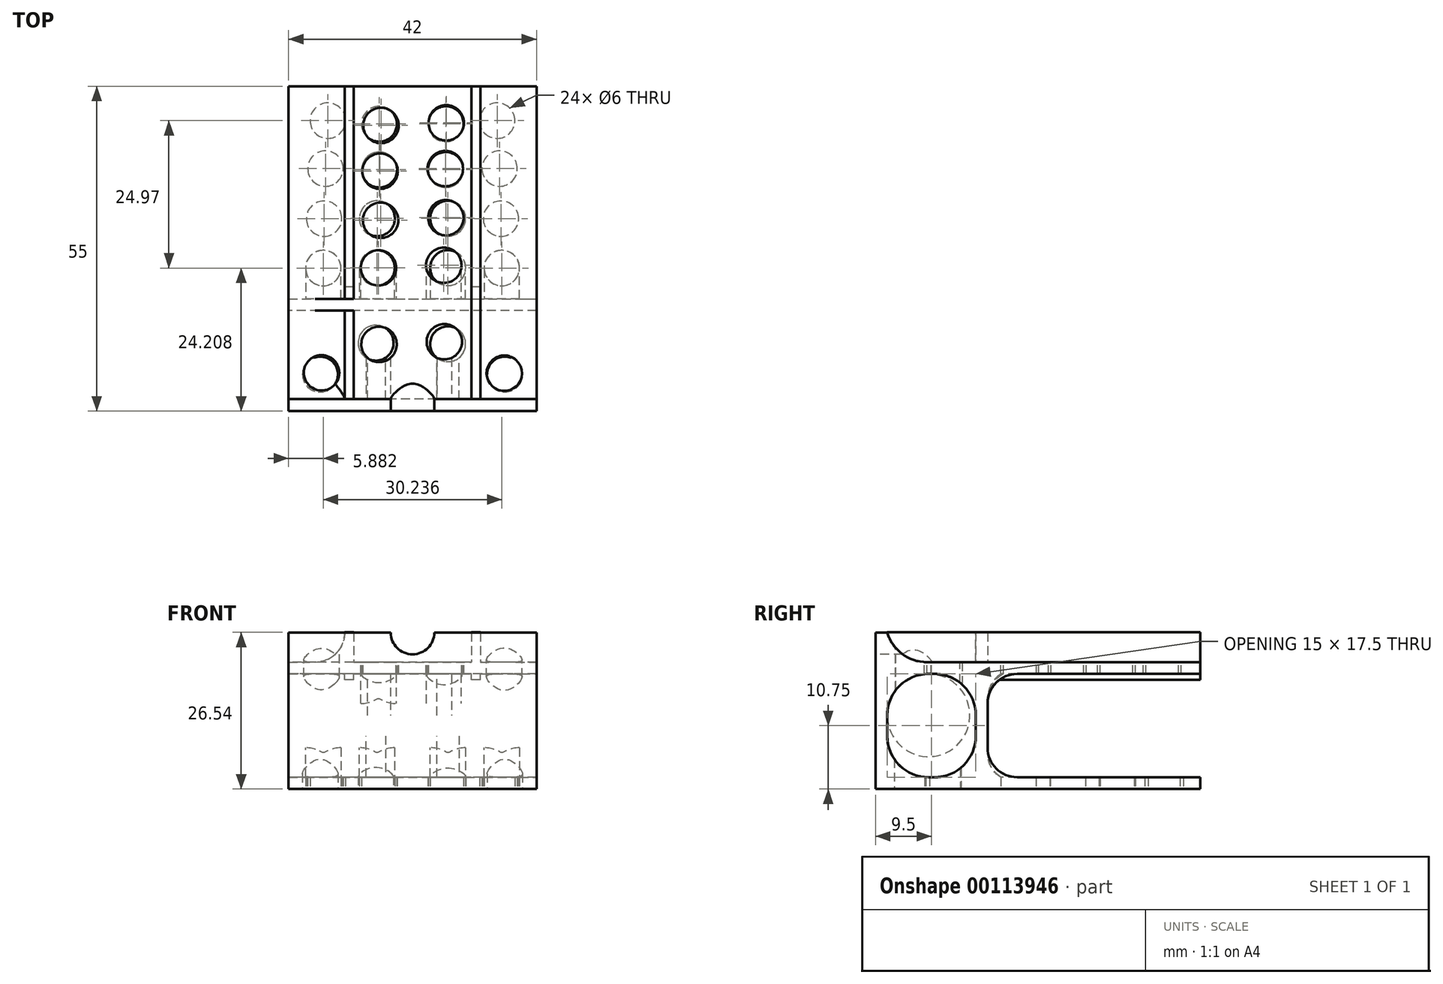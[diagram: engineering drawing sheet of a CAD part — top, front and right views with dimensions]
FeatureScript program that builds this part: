
annotation { "Feature Type Name" : "Feature", "Feature Type Description" : "" }
export const myFeature = defineFeature(function(context is Context, id is Id, definition is map)
    precondition{}
    {
        {
            var Q0;
            Q0=qCreatedBy(makeId("Front.planeOp"),FACE);
            var sketch = newSketch(context, id + "F0", { "sketchPlane" : qUnion([Q0])});
            skLineSegment(sketch, "E0.top", {"start": v(21, 15.75) * mm, "end": v(3.68, 15.75) * mm});
            skLineSegment(sketch, "E0.left", {"start": v(21, -10.75) * mm, "end": v(21, 15.75) * mm});
            skLineSegment(sketch, "E0.right", {"start": v(-21, -10.75) * mm, "end": v(-21, 15.75) * mm});
            skPoint(sketch, "E0.middle", {"position": v(0, 0) * mm});
            skLineSegment(sketch, "E1.bottom", {"start": v(21, -8.75) * mm, "end": v(-21, -8.75) * mm});
            skLineSegment(sketch, "E1.top", {"start": v(21, 8.75) * mm, "end": v(-21, 8.75) * mm});
            skLineSegment(sketch, "E1.left", {"start": v(21, -8.75) * mm, "end": v(21, 8.75) * mm});
            skLineSegment(sketch, "E1.right", {"start": v(-21, -8.75) * mm, "end": v(-21, 8.75) * mm});
            skLineSegment(sketch, "E2.bottom", {"start": v(21, -10.75) * mm, "end": v(-21, -10.75) * mm});
            skLineSegment(sketch, "E2.top", {"start": v(21, 10.75) * mm, "end": v(-21, 10.75) * mm});
            skLineSegment(sketch, "E2.left", {"start": v(21, -10.75) * mm, "end": v(21, 10.75) * mm});
            skLineSegment(sketch, "E2.right", {"start": v(-21, -10.75) * mm, "end": v(-21, 10.75) * mm});
            skArc(sketch, "E3", {"start": v(-3.68, 15.75) * mm, "mid": v(0, 12.07) * mm, "end": v(3.68, 15.75) * mm});
            skLineSegment(sketch, "E4.trimOffspring", {"start": v(-3.68, 15.75) * mm, "end": v(-21, 15.75) * mm});
            skPoint(sketch, "E5.orphan", {"position": v(-21, -15.75) * mm});
            skPoint(sketch, "E6.orphan", {"position": v(21, -15.75) * mm});
            skSolve(sketch);
        }
        {
            var Q0;
            Q0=qSketchRegion(id+"F0",true);
            extrude(context, id + "F1", {"entities" : qUnion([Q0]), "oppositeDirection" : true, "depth" : 2 * mm});
        }
        {
            var Q0;
            {var subQ0=sQuery(id+"F0.wireOp",EDGE,"E1.top");Q0=makeQuery(id+"F0.imprint","IMPRINT",FACE,{"disambiguationData":[TD([[makeQuery(id+"F0.imprint","IMPRINT",EDGE,{"derivedFrom":subQ0}),-1.0]])]});}
            var Q1;
            {var subQ0=sQuery(id+"F0.wireOp",EDGE,"E1.bottom");Q1=makeQuery(id+"F0.imprint","IMPRINT",FACE,{"disambiguationData":[TD([[makeQuery(id+"F0.imprint","IMPRINT",EDGE,{"derivedFrom":subQ0}),1.0]])]});}
            extrude(context, id + "F2", {"entities" : qUnion([Q0, Q1]), "operationType" : NewBodyOperationType.ADD, "oppositeDirection" : true, "depth" : 55 * mm});
        }
        {
            var Q0;
            Q0=makeQuery(id+"F2.opExtrude","SWEPT_FACE",FACE,{"disambiguationData":[OSD([sQuery(id+"F0.wireOp",EDGE,"E2.top")])]});
            var sketch = newSketch(context, id + "F3", { "sketchPlane" : qUnion([Q0])});
            skLineSegment(sketch, "E7.bottom", {"start": v(21, 2) * mm, "end": v(-21, 2) * mm});
            skLineSegment(sketch, "E7.top", {"start": v(21, 17) * mm, "end": v(-21, 17) * mm});
            skPoint(sketch, "E7.middle", {"position": v(0, 9.5) * mm});
            skLineSegment(sketch, "E8", {"start": v(-21, 19) * mm, "end": v(21, 19) * mm});
            skLineSegment(sketch, "E9", {"start": v(0, 55) * mm, "end": v(0, 0) * mm, "construction": true});
            skLineSegment(sketch, "E10.bottom", {"start": v(-11.49, 55) * mm, "end": v(-9.99, 55) * mm});
            skLineSegment(sketch, "E10.top", {"start": v(-11.49, 19) * mm, "end": v(-9.99, 19) * mm});
            skLineSegment(sketch, "E10.left", {"start": v(-11.49, 55) * mm, "end": v(-11.49, 19) * mm});
            skLineSegment(sketch, "E10.right", {"start": v(-9.99, 55) * mm, "end": v(-9.99, 19) * mm});
            skLineSegment(sketch, "E11.MirrorCS", {"start": v(9.99, 55) * mm, "end": v(9.99, 19) * mm});
            skLineSegment(sketch, "E12.MirrorCS", {"start": v(11.49, 55) * mm, "end": v(11.49, 19) * mm});
            skPoint(sketch, "E13.start.orphan", {"position": v(-19, 55) * mm});
            skPoint(sketch, "E14.MirrorCS.start.orphan", {"position": v(19, 55) * mm});
            skPoint(sketch, "E15.start.orphan", {"position": v(19, 19) * mm});
            skPoint(sketch, "E16.start.orphan", {"position": v(-19, 19) * mm});
            skLineSegment(sketch, "E17", {"start": v(-9.99, 19) * mm, "end": v(-9.99, 0) * mm});
            skLineSegment(sketch, "E18", {"start": v(-11.49, 19) * mm, "end": v(-11.49, 0) * mm});
            skLineSegment(sketch, "E19", {"start": v(9.99, 19) * mm, "end": v(9.99, 0) * mm});
            skLineSegment(sketch, "E20", {"start": v(11.49, 19) * mm, "end": v(11.49, 0) * mm});
            skSolve(sketch);
        }
        {
            var Q0;
            {var subQ0=sQuery(id+"F3.wireOp",EDGE,"E7.top");Q0=makeQuery(id+"F3.imprint","IMPRINT",FACE,{"disambiguationData":[TD([[makeQuery(id+"F3.imprint","IMPRINT",EDGE,{"derivedFrom":subQ0}),-1.0]])]});}
            var Q1;
            {var subQ0=sQuery(id+"F3.wireOp",EDGE,"E10.top");Q1=makeQuery(id+"F3.imprint","IMPRINT",FACE,{"disambiguationData":[TD([[makeQuery(id+"F3.imprint","IMPRINT",EDGE,{"derivedFrom":subQ0}),-1.0]])]});}
            extrude(context, id + "F4", {"entities" : qUnion([Q0, Q1]), "operationType" : NewBodyOperationType.ADD, "oppositeDirection" : true, "depth" : 21.22 * mm});
        }
        {
            var Q0;
            Q0=makeQuery(id+"F3.imprint","IMPRINT",FACE,{"disambiguationData":[TD([[makeQuery(id+"F3.imprint","IMPRINT",EDGE,{"derivedFrom":sQuery(id+"F3.wireOp",EDGE,"E10.bottom")}),1.0]])]});
            var Q1;
            {var subQ0=sQuery(id+"F3.wireOp",EDGE,"E11.MirrorCS");Q1=makeQuery(id+"F3.imprint","IMPRINT",FACE,{"disambiguationData":[TD([[makeQuery(id+"F3.imprint","IMPRINT",EDGE,{"derivedFrom":subQ0}),1.0]])]});}
            extrude(context, id + "F5", {"entities" : qUnion([Q0, Q1]), "operationType" : NewBodyOperationType.ADD, "oppositeDirection" : true, "depth" : 3 * mm});
        }
        {
            var Q0;
            {var subQ2=sQuery(id+"F0.wireOp",EDGE,"E2.bottom");Q0=makeQuery(id+"F4.boolean.opBoolean","SPLIT",FACE,{"disambiguationData":[TD([makeQuery(id+"F4.opExtrude","SWEPT_FACE",FACE,{"disambiguationData":[OSD([sQuery(id+"F3.wireOp",EDGE,"E8"),sQuery(id+"F3.wireOp",EDGE,"E10.top")])]})])],"derivedFrom":makeQuery(id+"F2.opExtrude","SWEPT_FACE",FACE,{"disambiguationData":[OSD([subQ2])]})});}
            var sketch = newSketch(context, id + "F6", { "sketchPlane" : qUnion([Q0])});
            skCircle(sketch, "E21", {"center": v(-15.12, -24.2) * mm, "radius": 3 * mm});
            skCircle(sketch, "E22", {"center": v(-6, -24.24) * mm, "radius": 3 * mm});
            skCircle(sketch, "E23", {"center": v(-14.98, -32.58) * mm, "radius": 3 * mm});
            skCircle(sketch, "E24", {"center": v(-6, -32.6) * mm, "radius": 3 * mm});
            skCircle(sketch, "E25", {"center": v(-5.62, -40.86) * mm, "radius": 3 * mm});
            skCircle(sketch, "E26", {"center": v(-14.75, -41.06) * mm, "radius": 3 * mm});
            skCircle(sketch, "E27", {"center": v(-14.35, -49.18) * mm, "radius": 3 * mm});
            skCircle(sketch, "E28", {"center": v(-5.65, -48.61) * mm, "radius": 3 * mm});
            skCircle(sketch, "E29", {"center": v(-15.63, -6.2) * mm, "radius": 3 * mm});
            skLineSegment(sketch, "E30", {"start": v(0, 29.9) * mm, "end": v(0, -70.72) * mm, "construction": true});
            skCircle(sketch, "E31.MirrorC", {"center": v(5.65, -48.61) * mm, "radius": 3 * mm});
            skCircle(sketch, "E32.MirrorC", {"center": v(14.35, -49.18) * mm, "radius": 3 * mm});
            skCircle(sketch, "E33.MirrorC", {"center": v(14.75, -41.06) * mm, "radius": 3 * mm});
            skCircle(sketch, "E34.MirrorC", {"center": v(5.62, -40.86) * mm, "radius": 3 * mm});
            skCircle(sketch, "E35.MirrorC", {"center": v(6, -32.6) * mm, "radius": 3 * mm});
            skCircle(sketch, "E36.MirrorC", {"center": v(14.98, -32.58) * mm, "radius": 3 * mm});
            skCircle(sketch, "E37.MirrorC", {"center": v(15.12, -24.2) * mm, "radius": 3 * mm});
            skCircle(sketch, "E38.MirrorC", {"center": v(6, -24.24) * mm, "radius": 3 * mm});
            skCircle(sketch, "E39.MirrorC", {"center": v(15.63, -6.2) * mm, "radius": 3 * mm});
            skCircle(sketch, "E40", {"center": v(-6.21, -11.52) * mm, "radius": 3 * mm});
            skCircle(sketch, "E41", {"center": v(6, -11.35) * mm, "radius": 3 * mm});
            skSolve(sketch);
        }
        {
            var Q0;
            Q0=qSketchRegion(id+"F6",true);
            extrude(context, id + "F7", {"entities" : qUnion([Q0]), "operationType" : NewBodyOperationType.REMOVE, "oppositeDirection" : true, "depth" : 10 * mm});
        }
        {
            var Q0;
            {var subQ0=sQuery(id+"F3.wireOp",EDGE,"E10.right");Q0=makeQuery(id+"F3.imprint","IMPRINT",FACE,{"disambiguationData":[TD([[makeQuery(id+"F3.imprint","IMPRINT",EDGE,{"derivedFrom":subQ0}),1.0]])]});}
            var sketch = newSketch(context, id + "F8", { "sketchPlane" : qUnion([Q0])});
            skCircle(sketch, "E42", {"center": v(5.72, 48.8) * mm, "radius": 3 * mm});
            skCircle(sketch, "E43", {"center": v(-5.35, 48.36) * mm, "radius": 3 * mm});
            skCircle(sketch, "E44", {"center": v(5.56, 41.05) * mm, "radius": 3 * mm});
            skCircle(sketch, "E45", {"center": v(-5.5, 40.6) * mm, "radius": 3 * mm});
            skCircle(sketch, "E46", {"center": v(5.65, 32.74) * mm, "radius": 3 * mm});
            skCircle(sketch, "E47", {"center": v(-5.41, 32.3) * mm, "radius": 3 * mm});
            skCircle(sketch, "E48", {"center": v(5.3, 24.69) * mm, "radius": 3 * mm});
            skCircle(sketch, "E49", {"center": v(-5.76, 24.24) * mm, "radius": 3 * mm});
            skCircle(sketch, "E50", {"center": v(5.39, 11.73) * mm, "radius": 3 * mm});
            skCircle(sketch, "E51", {"center": v(-5.67, 11.29) * mm, "radius": 3 * mm});
            skCircle(sketch, "E52", {"center": v(-15.4, 6.47) * mm, "radius": 3 * mm});
            skCircle(sketch, "E53", {"center": v(15.54, 6.4) * mm, "radius": 3 * mm});
            skSolve(sketch);
        }
        {
            var Q0;
            Q0=qSketchRegion(id+"F8",true);
            extrude(context, id + "F9", {"entities" : qUnion([Q0]), "operationType" : NewBodyOperationType.REMOVE, "oppositeDirection" : true, "depth" : 10 * mm});
        }
        {
            var Q0;
            {var subQ0=sQuery(id+"F3.wireOp",EDGE,"E20");var subQ1=sQuery(id+"F3.wireOp",EDGE,"E7.bottom");var subQ2=makeQuery(id+"F3.imprint","INTERSECT",VERTEX,{"derivedFrom":[subQ1,subQ0]});Q0=makeQuery(id+"F3.imprint","IMPRINT",FACE,{"disambiguationData":[TD([[makeQuery(id+"F3.imprint","IMPRINT",EDGE,{"disambiguationData":[TD([[subQ2,-1.0]])],"derivedFrom":subQ1}),-1.0]])]});}
            var Q1;
            {var subQ0=sQuery(id+"F3.wireOp",EDGE,"E11.MirrorCS");Q1=makeQuery(id+"F3.imprint","IMPRINT",FACE,{"disambiguationData":[TD([[makeQuery(id+"F3.imprint","IMPRINT",EDGE,{"derivedFrom":subQ0}),1.0]])]});}
            var Q2;
            {var subQ0=sQuery(id+"F3.wireOp",EDGE,"E20");var subQ1=sQuery(id+"F3.wireOp",EDGE,"E7.top");var subQ2=makeQuery(id+"F3.imprint","INTERSECT",VERTEX,{"derivedFrom":[subQ1,subQ0]});Q2=makeQuery(id+"F3.imprint","IMPRINT",FACE,{"disambiguationData":[TD([[makeQuery(id+"F3.imprint","IMPRINT",EDGE,{"disambiguationData":[TD([[subQ2,-1.0]])],"derivedFrom":subQ1}),-1.0]])]});}
            var Q3;
            {var subQ0=sQuery(id+"F3.wireOp",EDGE,"E17");var subQ1=sQuery(id+"F3.wireOp",EDGE,"E7.bottom");var subQ2=makeQuery(id+"F3.imprint","INTERSECT",VERTEX,{"derivedFrom":[subQ1,subQ0]});Q3=makeQuery(id+"F3.imprint","IMPRINT",FACE,{"disambiguationData":[TD([[makeQuery(id+"F3.imprint","IMPRINT",EDGE,{"disambiguationData":[TD([[subQ2,-1.0]])],"derivedFrom":subQ1}),-1.0]])]});}
            var Q4;
            {var subQ5=sQuery(id+"F3.wireOp",EDGE,"E10.top");Q4=makeQuery(id+"F3.imprint","IMPRINT",FACE,{"disambiguationData":[TD([[makeQuery(id+"F3.imprint","IMPRINT",EDGE,{"derivedFrom":subQ5}),-1.0]])]});}
            var Q5;
            Q5=makeQuery(id+"F3.imprint","IMPRINT",FACE,{"disambiguationData":[TD([[makeQuery(id+"F3.imprint","IMPRINT",EDGE,{"derivedFrom":sQuery(id+"F3.wireOp",EDGE,"E10.bottom")}),1.0]])]});
            extrude(context, id + "F10", {"entities" : qUnion([Q0, Q1, Q2, Q3, Q4, Q5]), "operationType" : NewBodyOperationType.ADD, "depth" : 5.04 * mm});
        }
        {
            var Q0;
            Q0=makeQuery(id+"F4.boolean.opBoolean","INTERSECT",EDGE,{"derivedFrom":[makeQuery(id+"F2.opExtrude","SWEPT_FACE",FACE,{"disambiguationData":[OSD([sQuery(id+"F0.wireOp",EDGE,"E1.bottom")])]}),makeQuery(id+"F4.opExtrude","SWEPT_FACE",FACE,{"disambiguationData":[OSD([sQuery(id+"F3.wireOp",EDGE,"E7.top")])]})]});
            var Q1;
            Q1=makeQuery(id+"F2.boolean.opBoolean","INTERSECT",EDGE,{"derivedFrom":[makeQuery(id+"F1.opExtrude","CAP_FACE",FACE,{"disambiguationData":[OSD([sQuery(id+"F0.wireOp",EDGE,"E0.top"),sQuery(id+"F0.wireOp",EDGE,"E0.left"),sQuery(id+"F0.wireOp",EDGE,"E0.right"),sQuery(id+"F0.wireOp",EDGE,"E2.bottom"),sQuery(id+"F0.wireOp",EDGE,"E2.left"),sQuery(id+"F0.wireOp",EDGE,"E2.right"),sQuery(id+"F0.wireOp",EDGE,"E3"),sQuery(id+"F0.wireOp",EDGE,"E4.trimOffspring")])],"isStart":false}),makeQuery(id+"F2.opExtrude","SWEPT_FACE",FACE,{"disambiguationData":[OSD([sQuery(id+"F0.wireOp",EDGE,"E1.bottom")])]})]});
            var Q2;
            Q2=makeQuery(id+"F4.boolean.opBoolean","INTERSECT",EDGE,{"derivedFrom":[makeQuery(id+"F2.opExtrude","SWEPT_FACE",FACE,{"disambiguationData":[OSD([sQuery(id+"F0.wireOp",EDGE,"E1.top")])]}),makeQuery(id+"F4.opExtrude","SWEPT_FACE",FACE,{"disambiguationData":[OSD([sQuery(id+"F3.wireOp",EDGE,"E7.top")])]})]});
            var Q3;
            Q3=makeQuery(id+"F2.boolean.opBoolean","INTERSECT",EDGE,{"derivedFrom":[makeQuery(id+"F1.opExtrude","CAP_FACE",FACE,{"disambiguationData":[OSD([sQuery(id+"F0.wireOp",EDGE,"E0.top"),sQuery(id+"F0.wireOp",EDGE,"E0.left"),sQuery(id+"F0.wireOp",EDGE,"E0.right"),sQuery(id+"F0.wireOp",EDGE,"E2.bottom"),sQuery(id+"F0.wireOp",EDGE,"E2.left"),sQuery(id+"F0.wireOp",EDGE,"E2.right"),sQuery(id+"F0.wireOp",EDGE,"E3"),sQuery(id+"F0.wireOp",EDGE,"E4.trimOffspring")])],"isStart":false}),makeQuery(id+"F2.opExtrude","SWEPT_FACE",FACE,{"disambiguationData":[OSD([sQuery(id+"F0.wireOp",EDGE,"E1.top")])]})]});
            var Q4;
            Q4=makeQuery(id+"F2.boolean.opBoolean","INTERSECT",EDGE,{"derivedFrom":[makeQuery(id+"F1.opExtrude","CAP_FACE",FACE,{"disambiguationData":[OSD([sQuery(id+"F0.wireOp",EDGE,"E0.top"),sQuery(id+"F0.wireOp",EDGE,"E0.left"),sQuery(id+"F0.wireOp",EDGE,"E0.right"),sQuery(id+"F0.wireOp",EDGE,"E2.bottom"),sQuery(id+"F0.wireOp",EDGE,"E2.left"),sQuery(id+"F0.wireOp",EDGE,"E2.right"),sQuery(id+"F0.wireOp",EDGE,"E3"),sQuery(id+"F0.wireOp",EDGE,"E4.trimOffspring")])],"isStart":false}),makeQuery(id+"F2.opExtrude","SWEPT_FACE",FACE,{"disambiguationData":[OSD([sQuery(id+"F0.wireOp",EDGE,"E2.top")])]})]});
            fillet(context, id + "F11", {"entities" : qUnion([Q0, Q1, Q2, Q3, Q4]), "radius" : 7 * mm, "tangentPropagation" : true, "allowEdgeOverflow" : false});
        }
        {
            var Q0;
            Q0=makeQuery(id+"F10.opExtrude","CAP_EDGE",EDGE,{"disambiguationData":[OSD([sQuery(id+"F3.wireOp",EDGE,"E12.MirrorCS"),sQuery(id+"F3.wireOp",EDGE,"E20")])],"isStart":true});
            var Q1;
            Q1=makeQuery(id+"F10.opExtrude","CAP_EDGE",EDGE,{"disambiguationData":[OSD([sQuery(id+"F3.wireOp",EDGE,"E10.left"),sQuery(id+"F3.wireOp",EDGE,"E18")])],"isStart":true});
            var Q2;
            Q2=makeQuery(id+"F4.boolean.opBoolean","INTERSECT",EDGE,{"derivedFrom":[makeQuery(id+"F2.opExtrude","SWEPT_FACE",FACE,{"disambiguationData":[OSD([sQuery(id+"F0.wireOp",EDGE,"E1.bottom")])]}),makeQuery(id+"F4.opExtrude","SWEPT_FACE",FACE,{"disambiguationData":[OSD([sQuery(id+"F3.wireOp",EDGE,"E8"),sQuery(id+"F3.wireOp",EDGE,"E10.top")])]})]});
            var Q3;
            {var subQ3=sQuery(id+"F0.wireOp",EDGE,"E1.top");var subQ4=makeQuery(id+"F2.opExtrude","SWEPT_FACE",FACE,{"disambiguationData":[OSD([subQ3])]});var subQ5=makeQuery(id+"F4.opExtrude","SWEPT_FACE",FACE,{"disambiguationData":[OSD([sQuery(id+"F3.wireOp",EDGE,"E8"),sQuery(id+"F3.wireOp",EDGE,"E10.top")])]});Q3=makeQuery(id+"F5.boolean.opBoolean","SPLIT",EDGE,{"disambiguationData":[TD([makeQuery(id+"F5.opExtrude","SWEPT_FACE",FACE,{"disambiguationData":[OSD([sQuery(id+"F3.wireOp",EDGE,"E12.MirrorCS")])]})])],"derivedFrom":makeQuery(id+"F4.boolean.opBoolean","INTERSECT",EDGE,{"derivedFrom":[subQ4,subQ5]})});}
            var Q4;
            {var subQ0=sQuery(id+"F0.wireOp",EDGE,"E1.top");var subQ1=makeQuery(id+"F2.opExtrude","SWEPT_FACE",FACE,{"disambiguationData":[OSD([subQ0])]});var subQ5=makeQuery(id+"F4.opExtrude","SWEPT_FACE",FACE,{"disambiguationData":[OSD([sQuery(id+"F3.wireOp",EDGE,"E8"),sQuery(id+"F3.wireOp",EDGE,"E10.top")])]});Q4=makeQuery(id+"F5.boolean.opBoolean","SPLIT",EDGE,{"disambiguationData":[TD([makeQuery(id+"F5.opExtrude","SWEPT_FACE",FACE,{"disambiguationData":[OSD([sQuery(id+"F3.wireOp",EDGE,"E10.left")])]})])],"derivedFrom":makeQuery(id+"F4.boolean.opBoolean","INTERSECT",EDGE,{"derivedFrom":[subQ1,subQ5]})});}
            var Q5;
            {var subQ0=makeQuery(id+"F2.opExtrude","SWEPT_FACE",FACE,{"disambiguationData":[OSD([sQuery(id+"F0.wireOp",EDGE,"E1.top")])]});var subQ1=makeQuery(id+"F4.opExtrude","SWEPT_FACE",FACE,{"disambiguationData":[OSD([sQuery(id+"F3.wireOp",EDGE,"E8"),sQuery(id+"F3.wireOp",EDGE,"E10.top")])]});Q5=makeQuery(id+"F5.boolean.opBoolean","SPLIT",EDGE,{"disambiguationData":[TD([makeQuery(id+"F5.opExtrude","SWEPT_FACE",FACE,{"disambiguationData":[OSD([sQuery(id+"F3.wireOp",EDGE,"E10.right")])]})])],"derivedFrom":makeQuery(id+"F4.boolean.opBoolean","INTERSECT",EDGE,{"derivedFrom":[subQ0,subQ1]})});}
            fillet(context, id + "F12", {"entities" : qUnion([Q0, Q1, Q2, Q3, Q4, Q5]), "radius" : 5 * mm, "tangentPropagation" : true, "allowEdgeOverflow" : false});
        }
    });
